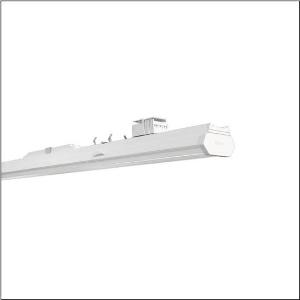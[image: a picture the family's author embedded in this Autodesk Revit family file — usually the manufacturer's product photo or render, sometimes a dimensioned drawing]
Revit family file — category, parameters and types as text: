
# Revit family: licross_r__11_protected_ho_51tp12cn4exm_ba42
name_source: partatom
category: Lighting Fixtures
units: mm (PartAtom-declared; Revit-internal decimal feet)

## family parameters
Cut with Voids When Loaded = No
Host = Face
Light Source = No
Part Type = Normal
Room Calculation Point = No
Round Connector Dimension = Use Diameter
Shared = No

## types (1)
- --- (1 x LED, 14240 lm, 77.6 W, 4000K)
    Apparent Load = 78 VA
    CIE Flux Codes = 70 91 97 98 100
    Color Rendering = 80
    Color Temperature = 4000K
    Default Elevation = 1800 mm
    Description = Licross® 11 Protected HO, luminaire insert, of sheet steel, galvanised, coil coated, white, length: 1.500mm, width: 90mm, height: 101mm, LED rated luminous flux: 14.240lm, light colour: 840, control gear: ON/OFF Multilumen, CLOi, with plug, 3-pole, with phase selection, mains connection: 220..240V, AC, 50/60Hz, start of lifetime: 78W, end of service life: 87W, halogen-free wiring, primary light control with lens, of plastic, primary optical cover: cover, of PMMA, light emission: direct distribution, primary light characteristic: symmetric, protection rating (complete): IP64, insulation class (complete): insulation class I (protective earthing), certification: CE, ENEC, VDE, UKCA, protection symbol: D if used in an environment with conductive dust loads with corresponding accessories, impact resistance: IK06, permissible ambient temperature for indoor applications: -35..+35°C, corresponds to IFS (International Featured Standards) requirements for safety and quality in the food industry, reducing of maximum allowable ambient temperature of 5°C with ceiling mounting, LABS conformity tested according to VDMA 24364:2018-05, packaging unit: 1 piece
    Height = 92 mm
    Lamp = 1 x LED
    Lamp Light Flux = 14240 lm
    Lamp Power = 77.6 W
    Lamp count = 1
    Length = 1500 mm
    Luminous efficacy = 184 lm/W
    Manufacturer = Siteco
    ModVariant = No
    Model = 51TP12CN4EXM
    Mounting Place = Ceiling
    Mounting Type = Pendant
    Number of Poles = 1
    OnlyDefault = Yes
    Power Factor = 1
    Product Name = Licross® 11 Protected HO
    Product group = luminaire insert
    ProductGroupID = 901
    Protection Class = Protection class I
    Protection Degree = IP 64
    RLX_Detail_Level = 1
    RLX_Emergency_Light_Flux = 0 lm
    RLX_Emergency_Type = 0
    RLX_Emergency_Type_DB = No
    RlxData = <blob elided: 22265 chars, md5=12653317>
    Socket = socket
    Standby Power = 0 W
    System Light Flux = 14240 lm
    System Power = 78 W
    Type Comments = factory setting: luminous flux: 100 % | (A | C | E) | 181 mA
    Type Image = l_1256148.jpg
    URL = http://relux.com
    VarID = @adj_019463
    Voltage = 0 V
    Weight = 0.00 kg
    Width = 88 mm

## geometry (parser evidence)
native form markers: Blend x4, Sweep x10
no freeform markers — native parametric forms only
